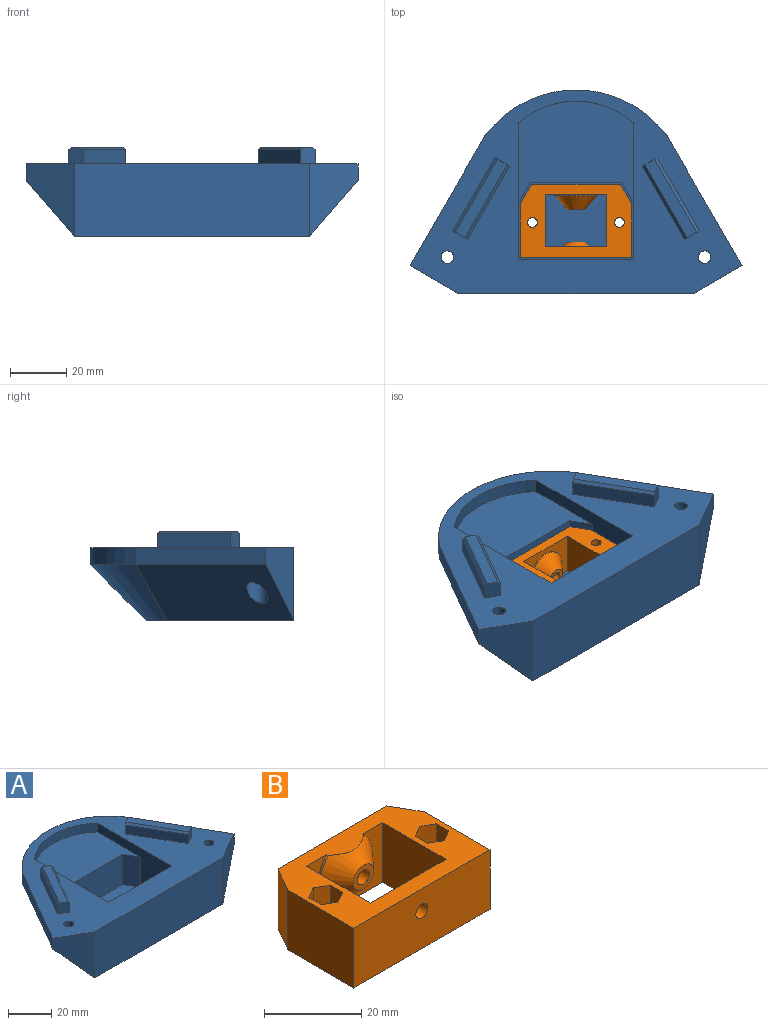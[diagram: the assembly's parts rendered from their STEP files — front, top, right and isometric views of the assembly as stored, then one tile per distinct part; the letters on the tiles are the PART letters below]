
ASSEMBLY  parts=2 mates=1
PART A: 46 faces, bbox 118.1x72.5x32 mm
  f0: plane 41x36.3mm, normal (0,0,1), area 1116.6mm2, adj f26,f27,f28,f36,f37,f38
  f1: plane 118.09x72.5mm, normal (0,0,1), area 3364.7mm2, adj f2,f3,f4,f5,f6,f7,f8,f9
  f2: cylinder r=2.25mm len=4.5mm, axis (0,0,1), area 56.5mm2, adj f1,f23
  f3: cylinder r=2.25mm len=4.5mm, axis (0,0,1), area 56.5mm2, adj f1,f22
  f4: plane 83.45x26mm, normal (0,-1,0), area 2169.6mm2, adj f1,f5,f9,f10
  f5: plane 26x17.32mm, normal (0.5,-0.87,0), area 320mm2, adj f1,f4,f6,f33
  f6: plane 46.19x26.67mm, normal (0.87,0.5,0), area 320mm2, adj f1,f5,f7,f33
  f7: cylinder r=40.29mm len=64.75mm, axis (0,0,1), area 451.2mm2, adj f1,f6,f8,f35
  f8: plane 46.19x26.67mm, normal (-0.87,0.5,0), area 320mm2, adj f1,f7,f9,f34
  f9: plane 26x17.32mm, normal (-0.5,-0.87,0), area 320mm2, adj f1,f4,f8,f34
  f10: plane 83.45x52.5mm, normal (0,0,-1), area 2693.8mm2, adj f4,f33,f34,f35,f42,f45
  f11: plane 6x5.2mm, normal (0.5,0.87,0), area 35mm2, adj f1,f12,f14,f15,f31,f32
  f12: plane 25.98x15mm, normal (-0.87,0.5,0), area 150mm2, adj f1,f11,f13,f32
  f13: plane 6x5.2mm, normal (-0.5,-0.87,0), area 35mm2, adj f1,f12,f14,f15,f31,f32
  f14: plane 25.98x15mm, normal (0.87,-0.5,0), area 150mm2, adj f1,f11,f13,f31
  f15: plane 27.98x18.46mm, normal (0,0,1), area 120mm2, adj f11,f13,f31,f32
  f16: plane 25.98x15mm, normal (0.87,0.5,0), area 150mm2, adj f1,f17,f19,f29
  f17: plane 6x5.2mm, normal (-0.5,0.87,0), area 35mm2, adj f1,f16,f18,f20,f29,f30
  f18: plane 25.98x15mm, normal (-0.87,-0.5,0), area 150mm2, adj f1,f17,f19,f30
  f19: plane 6x5.2mm, normal (0.5,-0.87,0), area 35mm2, adj f1,f16,f18,f20,f29,f30
  f20: plane 27.98x18.46mm, normal (0,0,1), area 120mm2, adj f17,f19,f29,f30
  f21: cylinder r=3.75mm len=15.75mm, axis (0,0,-1), area 282.7mm2, adj f22,f33
  f22: plane 7.5x7.5mm, normal (0,0,-1), area 28.3mm2, adj f3,f21
  f23: plane 7.5x7.5mm, normal (0,0,-1), area 28.3mm2, adj f2,f24
  f24: cylinder r=3.75mm len=15.75mm, axis (0,0,-1), area 282.7mm2, adj f23,f34
  f25: plane 41x22mm, normal (0,1,0), area 902mm2, adj f1,f26,f28,f39
  f26: plane 48.65x22mm, normal (-1,0,0), area 584.9mm2, adj f0,f1,f25,f27,f36,f39
  f27: cylinder r=31mm len=41mm, axis (0,0,1), area 224mm2, adj f0,f1,f26,f28
  f28: plane 48.65x22mm, normal (1,0,0), area 584.9mm2, adj f0,f1,f25,f27,f38,f39
  f29: plane 26.48x15.87mm, normal (0.61,0.35,0.71), area 42.4mm2, adj f16,f17,f19,f20
  f30: plane 26.48x15.87mm, normal (-0.61,-0.35,0.71), area 42.4mm2, adj f17,f18,f19,f20
  f31: plane 26.48x15.87mm, normal (0.61,-0.35,0.71), area 42.4mm2, adj f11,f13,f14,f15
  f32: plane 26.48x15.87mm, normal (-0.61,0.35,0.71), area 42.4mm2, adj f11,f12,f13,f15
  f33: plane 56.19x43.32mm, normal (0.61,0.35,-0.71), area 1428.3mm2, adj f5,f6,f10,f21,f35
  f34: plane 56.19x43.32mm, normal (-0.61,0.35,-0.71), area 1428.3mm2, adj f8,f9,f10,f24,f35
  f35: cone r=40.29mm half-angle=45deg, axis (0,0,1), area 1570.1mm2, adj f7,f10,f33,f34
  f36: plane 17x7.4mm, normal (-0.87,-0.5,0), area 145.4mm2, adj f0,f26,f37,f39
  f37: plane 32.45x17mm, normal (0,-1,0), area 551.6mm2, adj f0,f36,f38,f39
  f38: plane 17x7.4mm, normal (0.87,-0.5,0), area 145.4mm2, adj f0,f28,f37,f39
  f39: plane 41x27.5mm, normal (0,0,1), area 1076.6mm2, adj f25,f26,f28,f36,f37,f38,f40,f43
  f40: cylinder r=1.75mm len=3.5mm, axis (0,0,-1), area 22mm2, adj f39,f41
  f41: plane 6x6mm, normal (0,0,-1), area 18.7mm2, adj f40,f42
  f42: cylinder r=3mm len=6mm, axis (0,0,-1), area 37.7mm2, adj f10,f41
  f43: cylinder r=1.75mm len=3.5mm, axis (0,0,-1), area 22mm2, adj f39,f44
  f44: plane 6x6mm, normal (0,0,-1), area 18.7mm2, adj f43,f45
  f45: cylinder r=3mm len=6mm, axis (0,0,-1), area 37.7mm2, adj f10,f44
PART B: 37 faces, bbox 39.5x26x17 mm
  f0: cylinder r=7.5mm len=15mm, axis (0,1,0), area 18mm2, adj f3,f11,f32
  f1: cylinder r=1.75mm len=7.5mm, axis (0,0,-1), area 82.5mm2, adj f14,f28
  f2: cylinder r=1.75mm len=7.5mm, axis (0,0,-1), area 82.5mm2, adj f14,f21
  f3: plane 39.5x26mm, normal (0,0,1), area 546mm2, adj f0,f4,f5,f6,f7,f8,f9,f10
  f4: plane 31.58x15mm, normal (0,1,0), area 445.5mm2, adj f3,f5,f13,f14,f33
  f5: plane 15x6.86mm, normal (-0.87,0.5,0), area 118.7mm2, adj f3,f4,f6,f14
  f6: plane 19.14x15mm, normal (-1,0,0), area 287.2mm2, adj f3,f5,f7,f14
  f7: plane 39.5x15mm, normal (0,-1,0), area 582.9mm2, adj f3,f6,f8,f14,f36
  f8: plane 19.14x15mm, normal (1,0,0), area 287.2mm2, adj f3,f7,f13,f14
  f9: plane 22x15mm, normal (0,1,0), area 251.5mm2, adj f3,f10,f12,f14,f30
  f10: plane 18.5x15mm, normal (1,0,0), area 277.5mm2, adj f3,f9,f11,f14
  f11: plane 22x15mm, normal (0,-1,0), area 167.3mm2, adj f0,f3,f10,f12,f14
  f12: plane 18.5x15mm, normal (-1,0,0), area 277.5mm2, adj f3,f9,f11,f14
  f13: plane 15x6.86mm, normal (0.87,0.5,0), area 118.7mm2, adj f3,f4,f8,f14
  f14: plane 39.5x26mm, normal (0,0,-1), area 573.6mm2, adj f1,f2,f4,f5,f6,f7,f8,f9
  f15: plane 7.5x3.58mm, normal (-1,0,0), area 26.8mm2, adj f3,f16,f20,f21
  f16: plane 7.5x3.1mm, normal (-0.5,-0.87,0), area 26.8mm2, adj f3,f15,f17,f21
  f17: plane 7.5x3.1mm, normal (0.5,-0.87,0), area 26.8mm2, adj f3,f16,f18,f21
  f18: plane 7.5x3.58mm, normal (1,0,0), area 26.8mm2, adj f3,f17,f19,f21
  f19: plane 7.5x3.1mm, normal (0.5,0.87,0), area 26.8mm2, adj f3,f18,f20,f21
  f20: plane 7.5x3.1mm, normal (-0.5,0.87,0), area 26.8mm2, adj f3,f15,f19,f21
  f21: plane 7.16x6.2mm, normal (0,0,1), area 23.7mm2, adj f2,f15,f16,f17,f18,f19,f20
  f22: plane 7.5x3.58mm, normal (1,0,0), area 26.8mm2, adj f3,f23,f27,f28
  f23: plane 7.5x3.1mm, normal (0.5,0.87,0), area 26.8mm2, adj f3,f22,f24,f28
  f24: plane 7.5x3.1mm, normal (-0.5,0.87,0), area 26.8mm2, adj f3,f23,f25,f28
  f25: plane 7.5x3.58mm, normal (-1,0,0), area 26.8mm2, adj f3,f24,f26,f28
  f26: plane 7.5x3.1mm, normal (-0.5,-0.87,0), area 26.8mm2, adj f3,f25,f27,f28
  f27: plane 7.5x3.1mm, normal (0.5,-0.87,0), area 26.8mm2, adj f3,f22,f26,f28
  f28: plane 7.16x6.2mm, normal (0,0,1), area 23.7mm2, adj f1,f22,f23,f24,f25,f26,f27
  f29: plane 6x6mm, normal (0,1,0), area 18.7mm2, adj f30,f36
  f30: cone r=3mm half-angle=53.1deg, axis (0,-1,0), area 62.8mm2, adj f9,f29
  f31: plane 6x6mm, normal (0,-1,0), area 18.7mm2, adj f32,f35
  f32: cone r=3mm half-angle=42deg, axis (0,1,0), area 201mm2, adj f0,f3,f31
  f33: cylinder r=3mm len=6mm, axis (0,1,0), area 66mm2, adj f4,f34
  f34: plane 6x6mm, normal (0,1,0), area 18.7mm2, adj f33,f35
  f35: cylinder r=1.75mm len=5.5mm, axis (0,1,0), area 60.5mm2, adj f31,f34
  f36: cylinder r=1.75mm len=5.5mm, axis (0,1,0), area 60.5mm2, adj f7,f29
PLACE A t=(-0.5,-8.11,-8.69)mm
PLACE B rot(axis=(0,1,0),180deg) t=(-0.5,-8.08,-37.69)mm
MATE slider A.f39 <-> B.f3  axis (0,0,1) through (-0.5,-20.08,-30.69)mm
